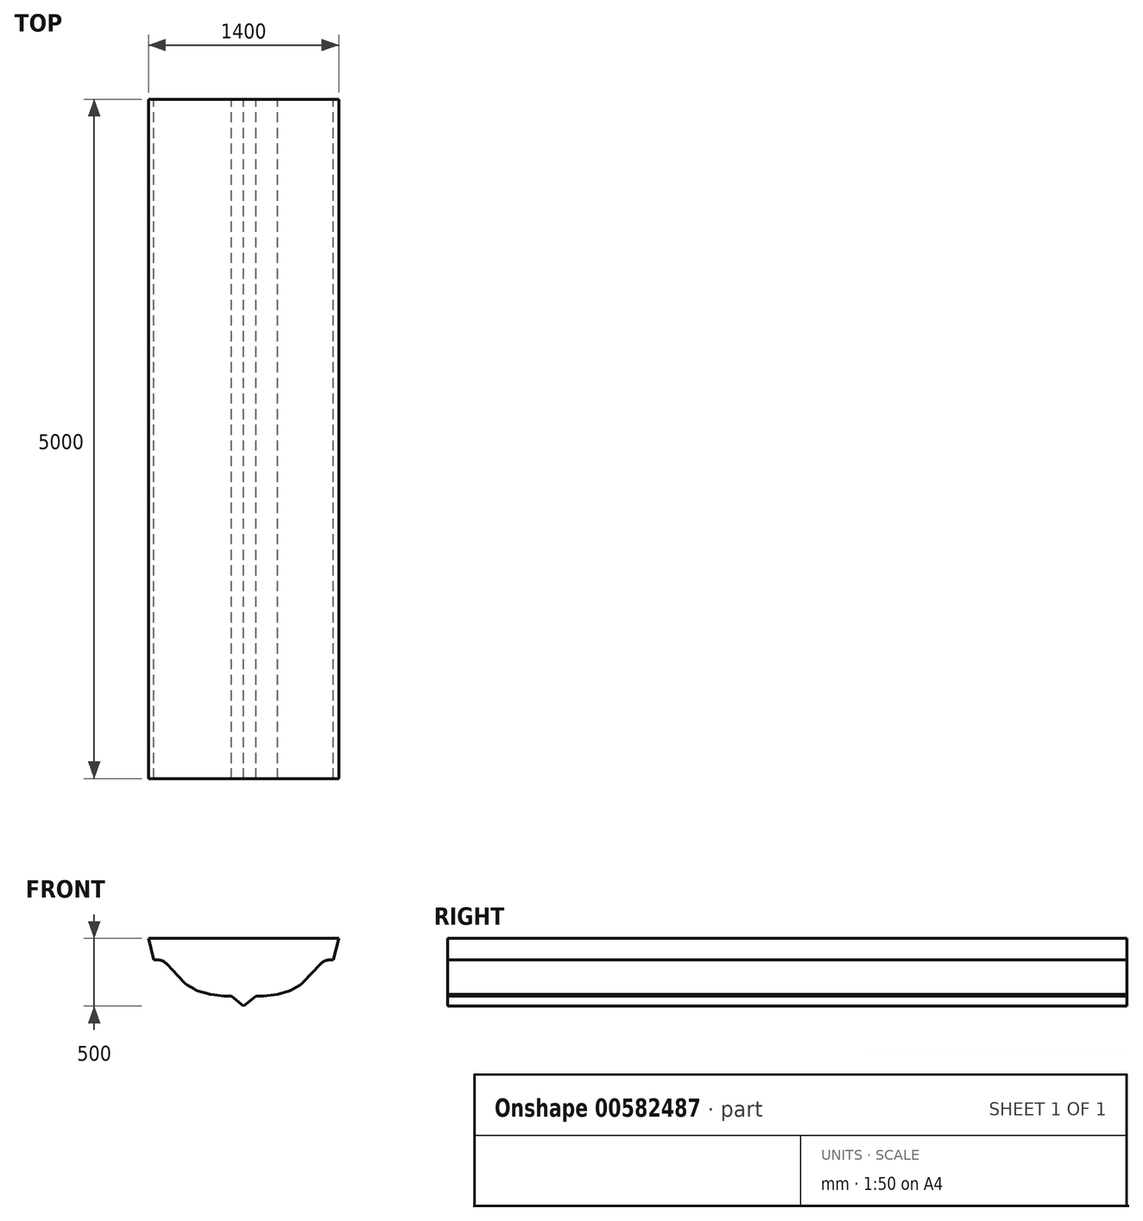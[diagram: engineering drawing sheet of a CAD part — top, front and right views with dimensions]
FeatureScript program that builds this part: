
annotation { "Feature Type Name" : "Feature", "Feature Type Description" : "" }
export const myFeature = defineFeature(function(context is Context, id is Id, definition is map)
    precondition{}
    {
        {
            var Q0;
            Q0=qCreatedBy(makeId("Front.planeOp"),FACE);
            var sketch = newSketch(context, id + "F0", { "sketchPlane" : qUnion([Q0])});
            skLineSegment(sketch, "E0", {"start": v(0, 0) * mm, "end": v(0, 500) * mm});
            skLineSegment(sketch, "E1", {"start": v(0, 500) * mm, "end": v(-700, 500) * mm});
            skLineSegment(sketch, "E2", {"start": v(0, 500) * mm, "end": v(700, 500) * mm});
            skLineSegment(sketch, "E3", {"start": v(-700, 500) * mm, "end": v(-659.97, 341.3) * mm});
            skLineSegment(sketch, "E4", {"start": v(-659.97, 341.3) * mm, "end": v(-636.6, 341.3) * mm});
            skLineSegment(sketch, "E5", {"start": v(-563.38, 309.42) * mm, "end": v(-438.5, 175.17) * mm});
            skLineSegment(sketch, "E6", {"start": v(-417.08, 157.74) * mm, "end": v(-360.72, 123.62) * mm});
            skLineSegment(sketch, "E7", {"start": v(-337.1, 113.2) * mm, "end": v(-256.35, 89.5) * mm});
            skLineSegment(sketch, "E8", {"start": v(-240.69, 86.24) * mm, "end": v(-144.68, 74.14) * mm});
            skLineSegment(sketch, "E9", {"start": v(-132.18, 73.35) * mm, "end": v(-90.3, 73.35) * mm});
            skLineSegment(sketch, "E10", {"start": v(-90.3, 73.35) * mm, "end": v(0, 0) * mm});
            skLineSegment(sketch, "E11.MirrorCS", {"start": v(90.3, 73.35) * mm, "end": v(0, 0) * mm});
            skLineSegment(sketch, "E12.MirrorCS", {"start": v(132.18, 73.35) * mm, "end": v(90.3, 73.35) * mm});
            skLineSegment(sketch, "E13.MirrorCS", {"start": v(248.65, 87.24) * mm, "end": v(144.68, 74.14) * mm});
            skLineSegment(sketch, "E14.MirrorCS", {"start": v(337.1, 113.2) * mm, "end": v(248.65, 87.24) * mm});
            skLineSegment(sketch, "E15.MirrorCS", {"start": v(417.08, 157.74) * mm, "end": v(360.72, 123.62) * mm});
            skLineSegment(sketch, "E16.MirrorCS", {"start": v(563.38, 309.42) * mm, "end": v(438.5, 175.17) * mm});
            skLineSegment(sketch, "E17.MirrorCS", {"start": v(659.97, 341.3) * mm, "end": v(636.6, 341.3) * mm});
            skLineSegment(sketch, "E18.MirrorCS", {"start": v(700, 500) * mm, "end": v(659.97, 341.3) * mm});
            skPoint(sketch, "E19.visualSharp", {"position": v(593.05, 341.3) * mm});
            skArc(sketch, "E19.filletArc", {"start": v(636.6, 341.3) * mm, "mid": v(596.67, 332.99) * mm, "end": v(563.38, 309.42) * mm});
            skPoint(sketch, "E20.visualSharp", {"position": v(-593.05, 341.3) * mm});
            skArc(sketch, "E20.filletArc", {"start": v(-563.38, 309.42) * mm, "mid": v(-596.67, 332.99) * mm, "end": v(-636.6, 341.3) * mm});
            skPoint(sketch, "E21.visualSharp", {"position": v(-349.58, 116.87) * mm});
            skArc(sketch, "E21.filletArc", {"start": v(-360.72, 123.62) * mm, "mid": v(-349.24, 117.65) * mm, "end": v(-337.1, 113.2) * mm});
            skPoint(sketch, "E22.visualSharp", {"position": v(-248.65, 87.24) * mm});
            skArc(sketch, "E22.filletArc", {"start": v(-256.35, 89.5) * mm, "mid": v(-248.58, 87.56) * mm, "end": v(-240.69, 86.24) * mm});
            skPoint(sketch, "E23.visualSharp", {"position": v(-429, 164.96) * mm});
            skArc(sketch, "E23.filletArc", {"start": v(-438.5, 175.17) * mm, "mid": v(-428.4, 165.71) * mm, "end": v(-417.08, 157.74) * mm});
            skPoint(sketch, "E24.visualSharp", {"position": v(-138.46, 73.35) * mm});
            skArc(sketch, "E24.filletArc", {"start": v(-144.68, 74.14) * mm, "mid": v(-138.44, 73.55) * mm, "end": v(-132.18, 73.35) * mm});
            skPoint(sketch, "E25.visualSharp", {"position": v(138.46, 73.35) * mm});
            skArc(sketch, "E25.filletArc", {"start": v(132.18, 73.35) * mm, "mid": v(138.44, 73.55) * mm, "end": v(144.68, 74.14) * mm});
            skPoint(sketch, "E26.visualSharp", {"position": v(349.58, 116.87) * mm});
            skArc(sketch, "E26.filletArc", {"start": v(337.1, 113.2) * mm, "mid": v(349.24, 117.65) * mm, "end": v(360.72, 123.62) * mm});
            skPoint(sketch, "E27.visualSharp", {"position": v(429, 164.96) * mm});
            skArc(sketch, "E27.filletArc", {"start": v(417.08, 157.74) * mm, "mid": v(428.4, 165.71) * mm, "end": v(438.5, 175.17) * mm});
            skSolve(sketch);
        }
        {
            var Q0;
            Q0=makeQuery(id+"F0.imprint","IMPRINT",FACE,{"disambiguationData":[TD([[makeQuery(id+"F0.imprint","IMPRINT",EDGE,{"derivedFrom":sQuery(id+"F0.wireOp",EDGE,"E0")}),-1.0]])]});
            cPlane(context, id + "F1", {"entities" : qUnion([Q0]), "cplaneType" : CPlaneType.OFFSET, "offset" : 1000 * mm, "width" : 150 * mm, "height" : 150 * mm});
        }
        {
            var Q0;
            Q0=makeQuery(id+"F0.imprint","IMPRINT",FACE,{"disambiguationData":[TD([[makeQuery(id+"F0.imprint","IMPRINT",EDGE,{"derivedFrom":sQuery(id+"F0.wireOp",EDGE,"E0")}),1.0]])]});
            var Q1;
            Q1=makeQuery(id+"F0.imprint","IMPRINT",FACE,{"disambiguationData":[TD([[makeQuery(id+"F0.imprint","IMPRINT",EDGE,{"derivedFrom":sQuery(id+"F0.wireOp",EDGE,"E0")}),-1.0]])]});
            extrude(context, id + "F2", {"entities" : qUnion([Q0, Q1]), "depth" : 5000 * mm, "offsetDistance" : 25 * mm});
        }
    });
